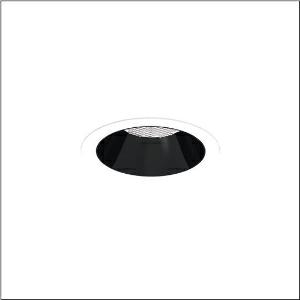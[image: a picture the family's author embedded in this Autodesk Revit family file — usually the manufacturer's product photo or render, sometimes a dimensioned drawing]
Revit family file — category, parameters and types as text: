
# Revit family: lunis_21_l_51db17md91c
name_source: partatom
category: Lighting Fixtures
units: mm (PartAtom-declared; Revit-internal decimal feet)

## family parameters
Cut with Voids When Loaded = No
Host = Face
Light Source = No
Part Type = Normal
Room Calculation Point = No
Round Connector Dimension = Use Diameter
Shared = No

## types (1)
- --- (1 x LED, 3200 lm, 21.7 W, 4000K)
    Apparent Load = 22 VA
    CIE Flux Codes = 90 99 100 100 100
    Color Rendering = 80
    Color Temperature = 4000K
    Default Elevation = 1800 mm
    Description = Lunis 21,  L, downlight, light control with lens, of PMMA, anti glare with reflector, of PC, light emission: direct distribution, LED rated luminous flux: 1.840lm, light colour: 830/840/865, with terminal, 3-pole, mains connection: 220..240V, AC/DC, 0/50..60Hz, housing, round, of diecast aluminium, traffic white (RAL 9016), diameter: 165mm, clamping range: 1..40mm, protection rating (complete): IP20, protection rating (on room side): IP54, insulation class (complete): insulation class II (safety insulation), certification: CE, impact resistance: IK03, packaging unit: 1 piece
    Height = 0 mm  [stored 0 ft]
    Lamp = 1 x LED
    Lamp Light Flux = 3200 lm
    Lamp Power = 21.7 W
    Lamp count = 1
    Length = 165 mm
    Luminous efficacy = 147 lm/W
    Manufacturer = Siteco
    ModVariant = No
    Model = 51DB17MD91C
    Mounting Place = Ceiling
    Mounting Type = Recessed
    Number of Poles = 1
    OnlyDefault = Yes
    Power Factor = 1
    Product Name = Lunis 21 L
    Product group = downlight
    ProductGroupID = 400
    Protection Class = Protection class II
    Protection Degree = IP 20
    RLX_Detail_Level = 1
    RLX_Emergency_Light_Flux = 0 lm
    RLX_Emergency_Type = 0
    RLX_Emergency_Type_DB = No
    RlxData = <blob elided: 14205 chars, md5=dc2b5cec>
    Socket = socket
    Standby Power = 0 W
    System Light Flux = 3200 lm
    System Power = 22 W
    Type Comments = individual setting: colour temperature 4000K, luminous flux: 100 % | (OFF | ON | ON | ON) | 650 mA
    Type Image = l_1291094.jpg
    URL = http://relux.com
    VarID = @adj_022305
    Voltage = 0 V
    Weight = 0.00 kg
    Width = 0 mm  [stored 0 ft]

note: [stored X ft] marks values corroborated as IEEE doubles in the binary element streams (Revit-internal decimal feet)

## geometry (parser evidence)
native form markers: Sweep x10
no freeform markers — native parametric forms only
